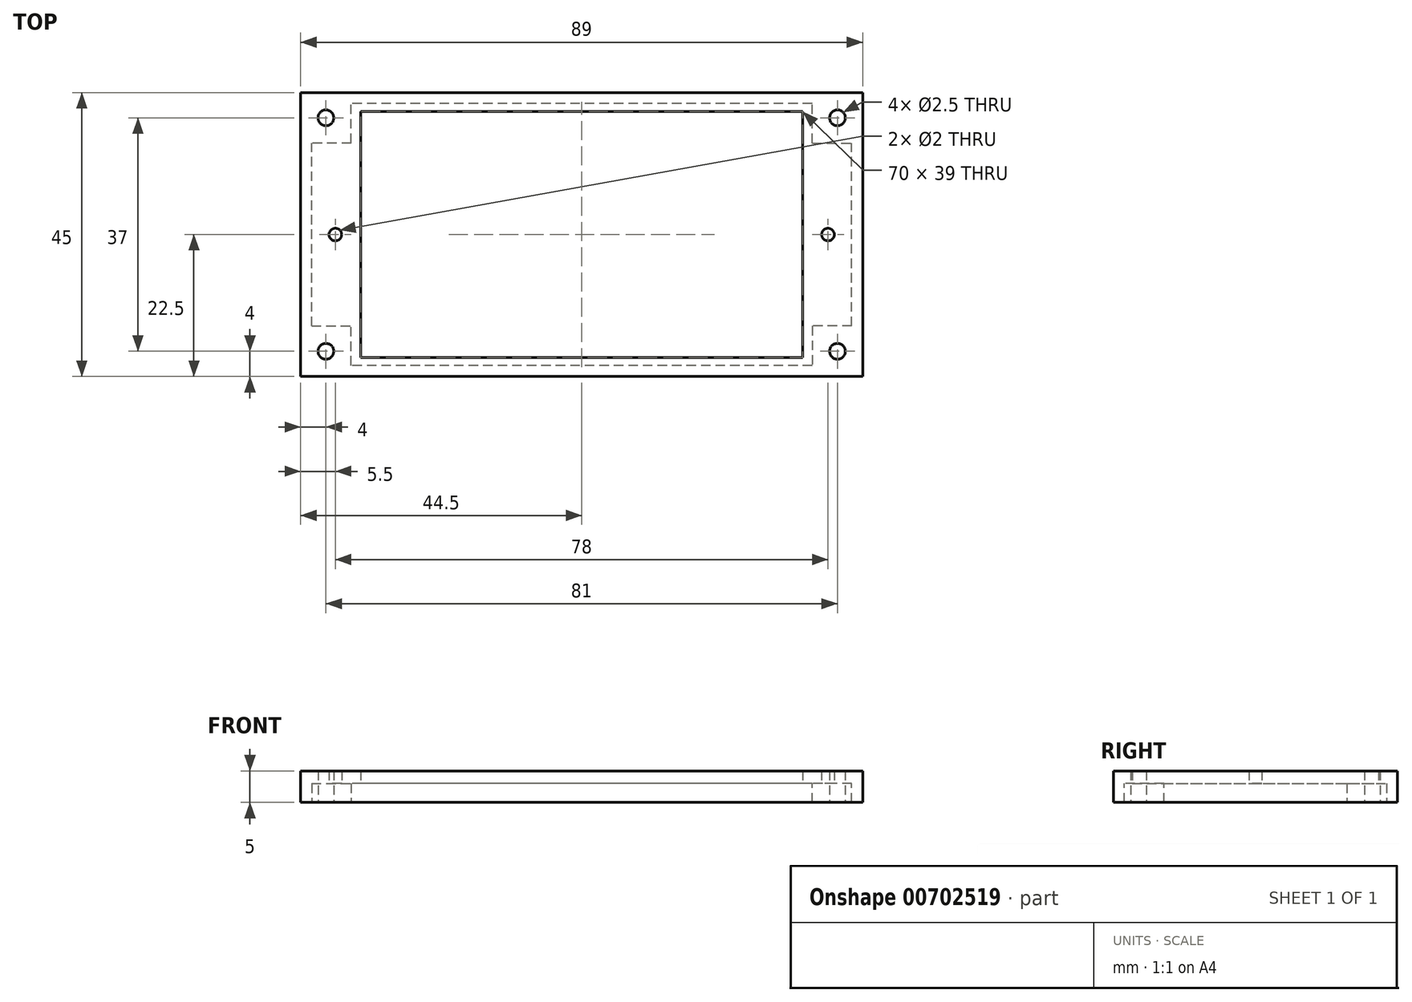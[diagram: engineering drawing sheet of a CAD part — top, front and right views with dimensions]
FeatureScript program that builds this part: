
annotation { "Feature Type Name" : "Feature", "Feature Type Description" : "" }
export const myFeature = defineFeature(function(context is Context, id is Id, definition is map)
    precondition{}
    {
        {
            var Q0;
            Q0=qCreatedBy(makeId("Top.planeOp"),FACE);
            var sketch = newSketch(context, id + "F0", { "sketchPlane" : qUnion([Q0])});
            skLineSegment(sketch, "E0.bottom", {"start": v(44.5, -22.5) * mm, "end": v(-44.5, -22.5) * mm});
            skLineSegment(sketch, "E0.top", {"start": v(44.5, 22.5) * mm, "end": v(-44.5, 22.5) * mm});
            skLineSegment(sketch, "E0.left", {"start": v(44.5, -22.5) * mm, "end": v(44.5, 22.5) * mm});
            skLineSegment(sketch, "E0.right", {"start": v(-44.5, -22.5) * mm, "end": v(-44.5, 22.5) * mm});
            skPoint(sketch, "E0.middle", {"position": v(0, 0) * mm});
            skSolve(sketch);
        }
        {
            var Q0;
            Q0 = qSketchRegion(id + "F0", true);
            extrude(context, id + "F1", {"entities" : qUnion([Q0]), "depth" : 5 * mm, "offsetDistance" : 25 * mm});
        }
        {
            var Q0;
            Q0=qCreatedBy(makeId("Top.planeOp"),FACE);
            var sketch = newSketch(context, id + "F2", { "sketchPlane" : qUnion([Q0])});
            skLineSegment(sketch, "E1.bottom", {"start": v(35, -19.5) * mm, "end": v(-35, -19.5) * mm});
            skLineSegment(sketch, "E1.top", {"start": v(35, 19.5) * mm, "end": v(-35, 19.5) * mm});
            skLineSegment(sketch, "E1.left", {"start": v(35, -19.5) * mm, "end": v(35, 19.5) * mm});
            skLineSegment(sketch, "E1.right", {"start": v(-35, -19.5) * mm, "end": v(-35, 19.5) * mm});
            skPoint(sketch, "E1.middle", {"position": v(0, 0) * mm});
            skSolve(sketch);
        }
        {
            var Q0;
            Q0 = qSketchRegion(id + "F2", true);
            extrude(context, id + "F3", {"entities" : qUnion([Q0]), "operationType" : NewBodyOperationType.REMOVE, "depth" : 25 * mm, "offsetDistance" : 25 * mm});
        }
        {
            var Q0;
            Q0=qCreatedBy(makeId("Top.planeOp"),FACE);
            var sketch = newSketch(context, id + "F4", { "sketchPlane" : qUnion([Q0])});
            skLineSegment(sketch, "E2.bottom", {"start": v(42.75, -20.75) * mm, "end": v(-42.75, -20.75) * mm});
            skLineSegment(sketch, "E2.top", {"start": v(42.75, 20.75) * mm, "end": v(-42.75, 20.75) * mm});
            skLineSegment(sketch, "E2.left", {"start": v(42.75, -20.75) * mm, "end": v(42.75, 20.75) * mm});
            skLineSegment(sketch, "E2.right", {"start": v(-42.75, -20.75) * mm, "end": v(-42.75, 20.75) * mm});
            skPoint(sketch, "E2.middle", {"position": v(0, 0) * mm});
            skSolve(sketch);
        }
        {
            var Q0;
            Q0 = qSketchRegion(id + "F4", true);
            extrude(context, id + "F5", {"entities" : qUnion([Q0]), "operationType" : NewBodyOperationType.REMOVE, "depth" : 3 * mm, "offsetDistance" : 25 * mm});
        }
        {
            var Q0;
            Q0=qCreatedBy(makeId("Top.planeOp"),FACE);
            var sketch = newSketch(context, id + "F6", { "sketchPlane" : qUnion([Q0])});
            skLineSegment(sketch, "E3.bottom", {"start": v(-36.5, 14.5) * mm, "end": v(-44.5, 14.5) * mm});
            skLineSegment(sketch, "E3.top", {"start": v(-36.5, 22.5) * mm, "end": v(-44.5, 22.5) * mm});
            skLineSegment(sketch, "E3.left", {"start": v(-36.5, 14.5) * mm, "end": v(-36.5, 22.5) * mm});
            skLineSegment(sketch, "E3.right", {"start": v(-44.5, 14.5) * mm, "end": v(-44.5, 22.5) * mm});
            skPoint(sketch, "E3.middle", {"position": v(-40.5, 18.5) * mm});
            skLineSegment(sketch, "E4.bottom", {"start": v(-44.5, -22.5) * mm, "end": v(-36.5, -22.5) * mm});
            skLineSegment(sketch, "E4.top", {"start": v(-44.5, -14.5) * mm, "end": v(-36.5, -14.5) * mm});
            skLineSegment(sketch, "E4.left", {"start": v(-44.5, -22.5) * mm, "end": v(-44.5, -14.5) * mm});
            skLineSegment(sketch, "E4.right", {"start": v(-36.5, -22.5) * mm, "end": v(-36.5, -14.5) * mm});
            skPoint(sketch, "E4.middle", {"position": v(-40.5, -18.5) * mm});
            skLineSegment(sketch, "E5.bottom", {"start": v(36.5, 14.5) * mm, "end": v(44.5, 14.5) * mm});
            skLineSegment(sketch, "E5.top", {"start": v(36.5, 22.5) * mm, "end": v(44.5, 22.5) * mm});
            skLineSegment(sketch, "E5.left", {"start": v(36.5, 14.5) * mm, "end": v(36.5, 22.5) * mm});
            skLineSegment(sketch, "E5.right", {"start": v(44.5, 14.5) * mm, "end": v(44.5, 22.5) * mm});
            skPoint(sketch, "E5.middle", {"position": v(40.5, 18.5) * mm});
            skLineSegment(sketch, "E6.bottom", {"start": v(44.5, -14.5) * mm, "end": v(36.5, -14.5) * mm});
            skLineSegment(sketch, "E6.top", {"start": v(44.5, -22.5) * mm, "end": v(36.5, -22.5) * mm});
            skLineSegment(sketch, "E6.left", {"start": v(44.5, -14.5) * mm, "end": v(44.5, -22.5) * mm});
            skLineSegment(sketch, "E6.right", {"start": v(36.5, -14.5) * mm, "end": v(36.5, -22.5) * mm});
            skSolve(sketch);
        }
        {
            var Q0;
            Q0 = qSketchRegion(id + "F6", true);
            extrude(context, id + "F7", {"entities" : qUnion([Q0]), "operationType" : NewBodyOperationType.ADD, "depth" : 3 * mm, "offsetDistance" : 25 * mm});
        }
        {
            var Q0;
            Q0=qCreatedBy(makeId("Top.planeOp"),FACE);
            var sketch = newSketch(context, id + "F8", { "sketchPlane" : qUnion([Q0])});
            skCircle(sketch, "E7", {"center": v(40.5, -18.5) * mm, "radius": 1.25 * mm});
            skCircle(sketch, "E8", {"center": v(40.5, 18.5) * mm, "radius": 1.25 * mm});
            skCircle(sketch, "E9", {"center": v(-40.5, -18.5) * mm, "radius": 1.25 * mm});
            skCircle(sketch, "E10", {"center": v(-40.5, 18.5) * mm, "radius": 1.25 * mm});
            skCircle(sketch, "E11", {"center": v(-39, 0) * mm, "radius": 1 * mm});
            skCircle(sketch, "E12", {"center": v(39, 0) * mm, "radius": 1 * mm});
            skSolve(sketch);
        }
        {
            var Q0;
            Q0 = qSketchRegion(id + "F8", true);
            extrude(context, id + "F9", {"entities" : qUnion([Q0]), "operationType" : NewBodyOperationType.REMOVE, "depth" : 25 * mm, "offsetDistance" : 25 * mm});
        }
    });
